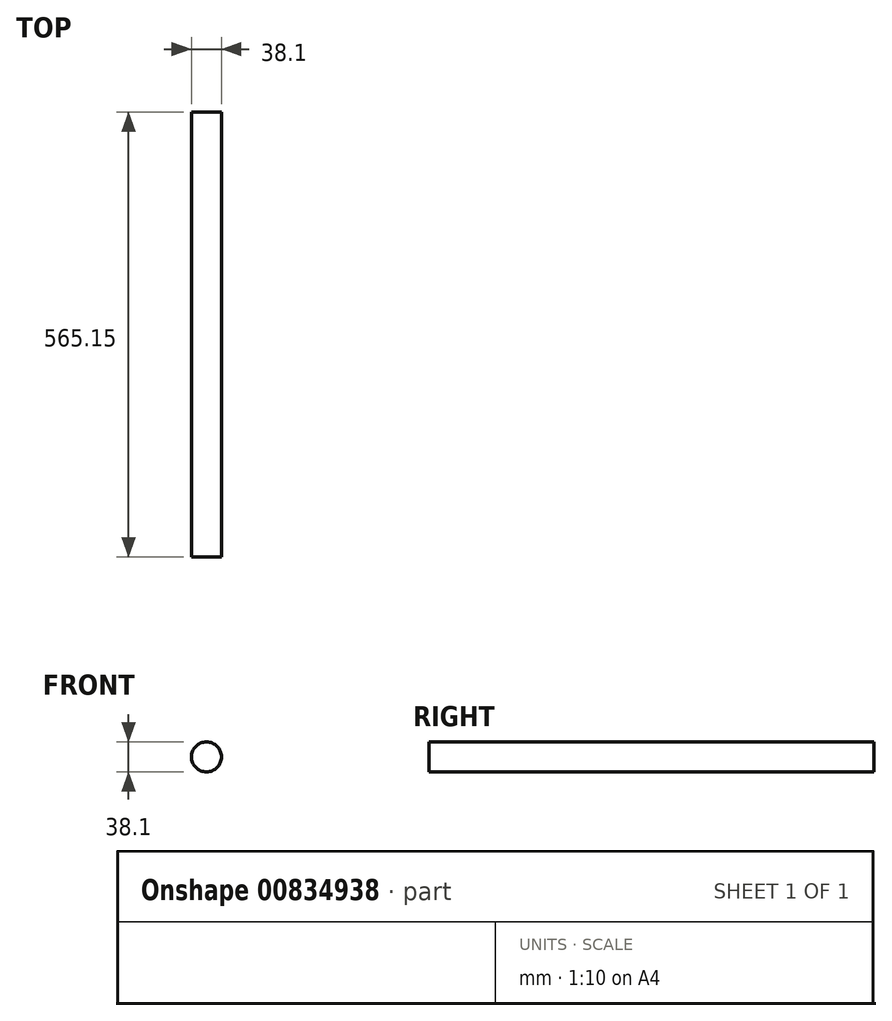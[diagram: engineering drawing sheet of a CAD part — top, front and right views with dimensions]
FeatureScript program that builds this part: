
annotation { "Feature Type Name" : "Feature", "Feature Type Description" : "" }
export const myFeature = defineFeature(function(context is Context, id is Id, definition is map)
    precondition{}
    {
        {
            var Q0;
            Q0=qCreatedBy(makeId("Front.planeOp"),FACE);
            var sketch = newSketch(context, id + "F0", { "sketchPlane" : qUnion([Q0])});
            skCircle(sketch, "E0", {"center": v(0, 0) * mm, "radius": 19.05 * mm});
            skSolve(sketch);
        }
        {
            var Q0;
            Q0 = qSketchRegion(id + "F0", true);
            extrude(context, id + "F1", {"entities" : qUnion([Q0]), "depth" : 565.15 * mm, "offsetDistance" : 25.4 * mm});
        }
    });
